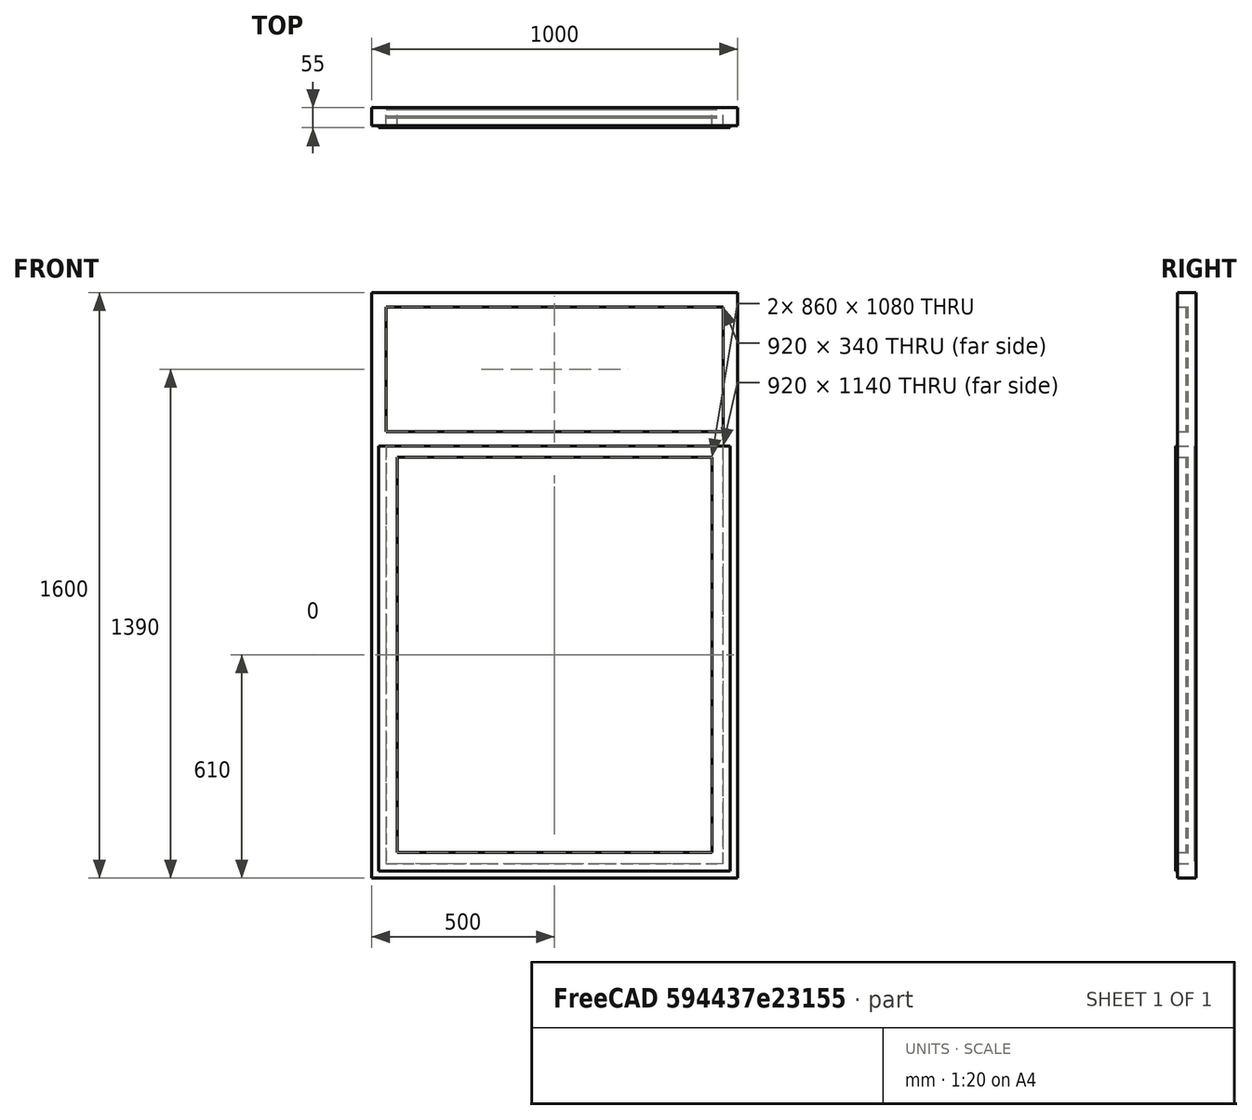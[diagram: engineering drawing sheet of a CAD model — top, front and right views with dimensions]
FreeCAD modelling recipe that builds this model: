
FCSTD DOCUMENT  (FreeCAD 0.16R6704 (Git))
Label: Maxim Air and fixed glass
License: CreativeCommons Attribution
LicenseURL: http://creativecommons.org/licenses/by/4.0/
objects: Sketcher::SketchObject×2, Part::FeaturePython×1, App::DocumentObjectGroup×1
note: 3 computed .brp shape members not serialized (recipe doc carries the construction recipe); baked Part::Feature solids carry a one-line shape summary decoded from their .brp

FEATURE [Sketcher::SketchObject] Sketch105
  Placement = pos=(0,0,0) rot=(1,0,0;1.5708rad)
  sketch-geometry (21):
    g0: LineSegment StartX=0 StartY=0 StartZ=0 EndX=1000 EndY=0 EndZ=0
    g1: LineSegment StartX=1000 StartY=0 StartZ=0 EndX=1000 EndY=1600 EndZ=0
    g2: LineSegment StartX=1000 StartY=1600 StartZ=0 EndX=0 EndY=1600 EndZ=0
    g3: LineSegment StartX=0 StartY=1600 StartZ=0 EndX=0 EndY=0 EndZ=0
    g4: LineSegment StartX=40 StartY=40 StartZ=0 EndX=960 EndY=40 EndZ=0
    g5: LineSegment StartX=960 StartY=40 StartZ=0 EndX=960 EndY=1180 EndZ=0
    g6: LineSegment StartX=960 StartY=1180 StartZ=0 EndX=40 EndY=1180 EndZ=0
    g7: LineSegment StartX=40 StartY=1180 StartZ=0 EndX=40 EndY=40 EndZ=0
    g8: LineSegment StartX=40 StartY=1560 StartZ=0 EndX=960 EndY=1560 EndZ=0
    g9: LineSegment StartX=960 StartY=1560 StartZ=0 EndX=960 EndY=1220 EndZ=0
    g10: LineSegment StartX=960 StartY=1220 StartZ=0 EndX=40 EndY=1220 EndZ=0
    g11: LineSegment StartX=40 StartY=1220 StartZ=0 EndX=40 EndY=1560 EndZ=0
    g12: LineSegment [constr] StartX=-307.315 StartY=1200 StartZ=0 EndX=1727 EndY=1200 EndZ=0
    g13: LineSegment StartX=70 StartY=1150 StartZ=0 EndX=930 EndY=1150 EndZ=0
    g14: LineSegment StartX=930 StartY=1150 StartZ=0 EndX=930 EndY=70 EndZ=0
    g15: LineSegment StartX=930 StartY=70 StartZ=0 EndX=70 EndY=70 EndZ=0
    g16: LineSegment StartX=70 StartY=70 StartZ=0 EndX=70 EndY=1150 EndZ=0
    g17: LineSegment StartX=20 StartY=1180 StartZ=0 EndX=980 EndY=1180 EndZ=0
    g18: LineSegment StartX=980 StartY=1180 StartZ=0 EndX=980 EndY=20 EndZ=0
    g19: LineSegment StartX=980 StartY=20 StartZ=0 EndX=20 EndY=20 EndZ=0
    g20: LineSegment StartX=20 StartY=20 StartZ=0 EndX=20 EndY=1180 EndZ=0
  constraints (61):
    c: Coincident(g0,g1)
    c: Coincident(g1,g2)
    c: Coincident(g2,g3)
    c: Coincident(g3,g0)
    c: Horizontal(g0)
    c: Horizontal(g2)
    c: Vertical(g1)
    c: Vertical(g3)
    c: Coincident(g4,g5)
    c: Coincident(g5,g6)
    c: Coincident(g6,g7)
    c: Coincident(g7,g4)
    c: Horizontal(g4)
    c: Horizontal(g6)
    c: Vertical(g5)
    c: Vertical(g7)
    c: DistanceX(g0) = 1000  'Largura do vão'
    c: DistanceX(g4,g0) = 40  'Largura perfil vertical 2'
    c: DistanceY(g0,g4) = 40  'Altura perfil inferior'
    c: Coincident(g0,g-1)
    c: Coincident(g8,g9)
    c: Coincident(g9,g10)
    c: Coincident(g10,g11)
    c: Coincident(g11,g8)
    c: Horizontal(g8)
    c: Horizontal(g10)
    c: Vertical(g9)
    c: Vertical(g11)
    c: DistanceX(g2,g8) = 40  'Largura perfil vertical 1'
    c: DistanceY(g8,g2) = 40  'Altura perfil superior'
    c: DistanceY(g6,g10) = 40  'Altura perfil bandeira'
    c: DistanceX(g9,g5) = 0  'Constraint32'
    c: Horizontal(g12)
    c: Symmetric(g9,g5,g12)
    c: DistanceY(g0,g1) = 1600  'Altura do vão'
    c: DistanceY(g0,g12) = 1200  'Altura vidro superior (eixo)'
    c: Coincident(g13,g14)
    c: Coincident(g14,g15)
    c: Coincident(g15,g16)
    c: Coincident(g16,g13)
    c: Horizontal(g13)
    c: Horizontal(g15)
    c: Vertical(g14)
    c: Vertical(g16)
    c: DistanceX(g6,g13) = 30  'Largura perfil vertical 1 maximar'
    c: DistanceY(g13,g6) = 30  'Altura perfil superior maximar'
    c: DistanceX(g13,g5) = 30  'largura perfil vertical 2 maximar'
    c: DistanceY(g4,g14) = 30  'Altura perfil inferior maximar'
    c: Coincident(g17,g18)
    c: Coincident(g18,g19)
    c: Coincident(g19,g20)
    c: Coincident(g20,g17)
    c: Horizontal(g17)
    c: Horizontal(g19)
    c: Vertical(g18)
    c: Vertical(g20)
    c: DistanceX(g4,g18) = 20  'Largura arremate vertical 2'
    c: DistanceY(g18,g4) = 20  'Altura arremate inferior'
    c: DistanceX(g19,g4) = 20  'Largura arremate vertical 1'
    c: DistanceY(g6,g17) = 0
    c: DistanceX(g10,g6) = 0
FEATURE [Part::FeaturePython] Window078  label="Maxim Air and fixed glass "  # WARN: FeaturePython — macro-defined, semantics opaque (R4)
  Base = -> Sketch105
  Height = 1000
  HoleDepth = 0
  MoveWithHost = true
  Normal = (0,1,0)
  Preset = 1
  Role = 0
  Width = 1000
  WindowParts = MONTANTES | Frame | Wire0,Wire1,Wire2 | 50.0 | 0.0 | MAXIMAR | Frame | Wire1,Wire3 | 45.0 | 0.0 | VIDRO 1 | Glass panel | Wire2 | 5.0 | 22.5 | ARREMATE | Frame | Wire4,Wire3 | 5.0 | -5.0 | VIDRO 2 | Glass panel | Wire3 | 5.0 | 22.5
FEATURE [Sketcher::SketchObject] Sketch106  label="Opening indication"
  ExternalGeometry = -> [Window078]
  Placement = pos=(0,22.5,0) rot=(1,0,0;1.5708rad)
  Support = -> Window078 [Face45]
  sketch-geometry (3):
    g0: LineSegment StartX=70 StartY=1150 StartZ=0 EndX=500 EndY=70 EndZ=0
    g1: LineSegment StartX=500 StartY=70 StartZ=0 EndX=930 EndY=1150 EndZ=0
    g2: LineSegment [constr] StartX=500 StartY=1376.58 StartZ=0 EndX=500 EndY=-196.594 EndZ=0
  constraints (7):
    c: Coincident(g-4,g0)
    c: PointOnObject(g0,g-5)
    c: Coincident(g0,g1)
    c: Coincident(g1,g-6)
    c: Vertical(g2)
    c: Symmetric(g1,g0,g2)
    c: PointOnObject(g0,g2)
FEATURE [App::DocumentObjectGroup] Grupo089  label="Maxim Air and fixed glass"
  Group = -> [Window078,Sketch106]
